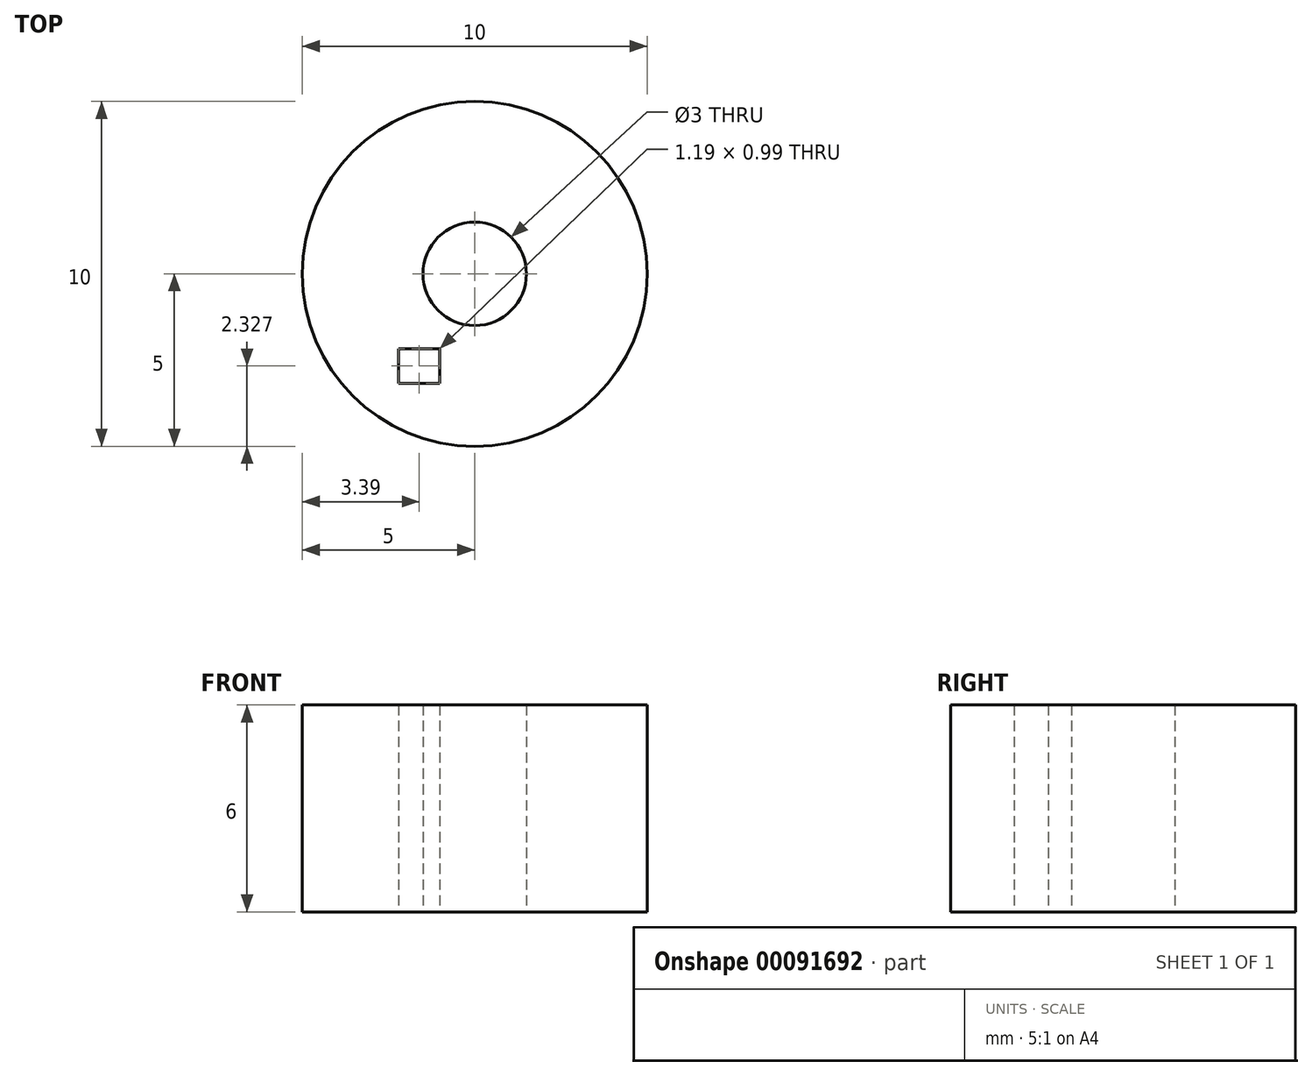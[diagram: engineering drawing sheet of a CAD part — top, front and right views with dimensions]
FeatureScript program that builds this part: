
annotation { "Feature Type Name" : "Feature", "Feature Type Description" : "" }
export const myFeature = defineFeature(function(context is Context, id is Id, definition is map)
    precondition{}
    {
        {
            var Q0;
            Q0=qCreatedBy(makeId("Top.planeOp"),FACE);
            var sketch = newSketch(context, id + "F0", { "sketchPlane" : qUnion([Q0])});
            skCircle(sketch, "E0", {"center": v(0, 0) * mm, "radius": 5 * mm});
            skCircle(sketch, "E1", {"center": v(0, 0) * mm, "radius": 1.5 * mm});
            skLineSegment(sketch, "E2.bottom", {"start": v(-2.2, -2.18) * mm, "end": v(-1.01, -2.18) * mm});
            skLineSegment(sketch, "E2.top", {"start": v(-2.2, -3.17) * mm, "end": v(-1.01, -3.17) * mm});
            skLineSegment(sketch, "E2.left", {"start": v(-2.2, -2.18) * mm, "end": v(-2.2, -3.17) * mm});
            skLineSegment(sketch, "E2.right", {"start": v(-1.01, -2.18) * mm, "end": v(-1.01, -3.17) * mm});
            skSolve(sketch);
        }
        {
            var Q0;
            Q0=makeQuery(id+"F0.imprint","IMPRINT",FACE,{"disambiguationData":[TD([[makeQuery(id+"F0.imprint","IMPRINT",EDGE,{"derivedFrom":sQuery(id+"F0.wireOp",EDGE,"E0")}),1.0]])]});
            extrude(context, id + "F1", {"entities" : qUnion([Q0]), "depth" : 6 * mm});
        }
    });
